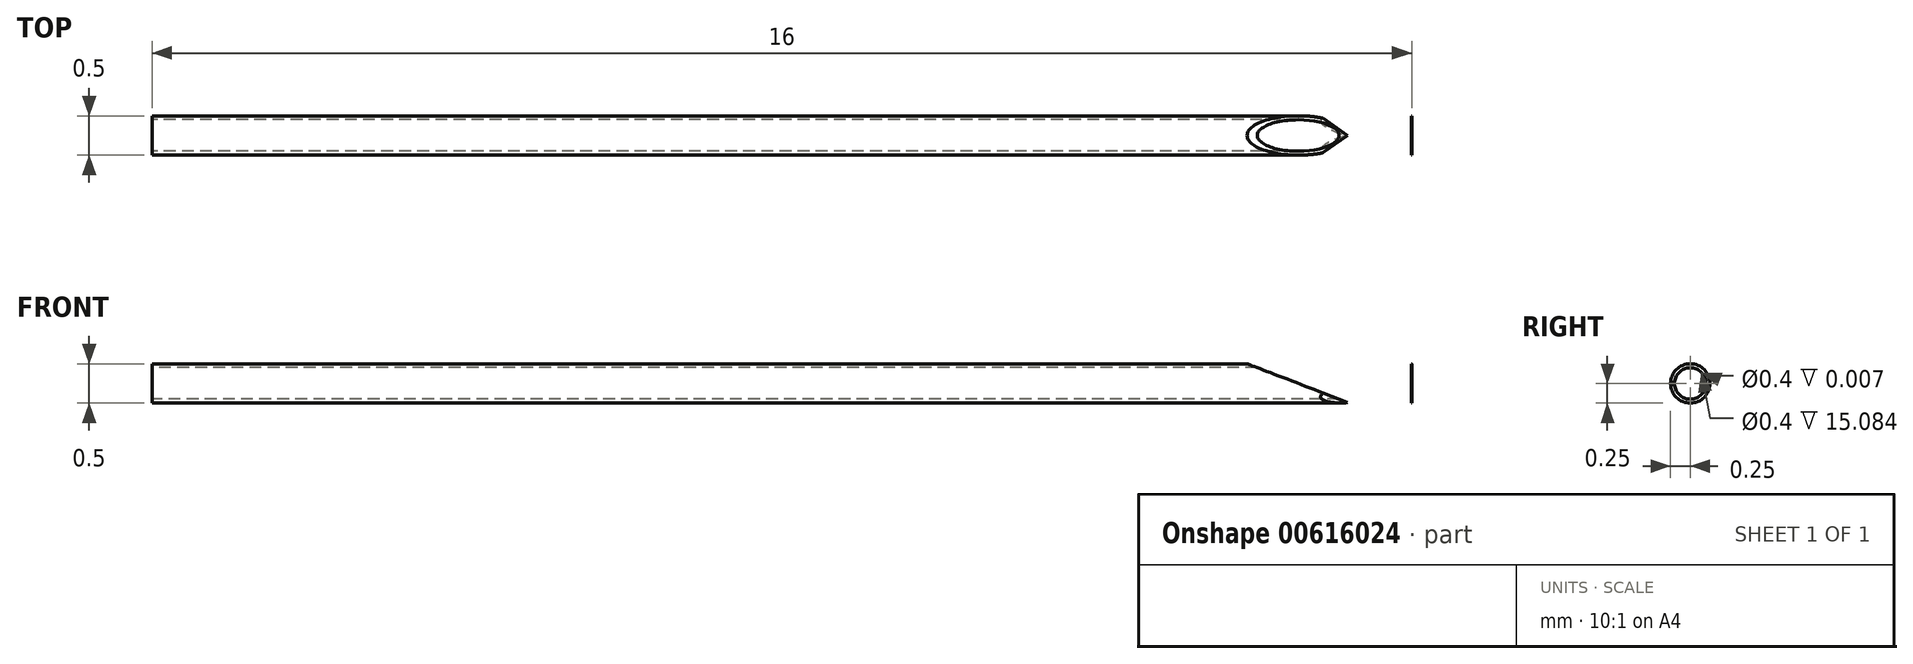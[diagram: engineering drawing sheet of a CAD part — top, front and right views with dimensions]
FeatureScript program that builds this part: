
annotation { "Feature Type Name" : "Feature", "Feature Type Description" : "" }
export const myFeature = defineFeature(function(context is Context, id is Id, definition is map)
    precondition{}
    {
        {
            var Q0;
            Q0=qCreatedBy(makeId("Front.planeOp"),FACE);
            var sketch = newSketch(context, id + "F0", { "sketchPlane" : qUnion([Q0])});
            skLineSegment(sketch, "E0", {"start": v(-2, 0) * mm, "end": v(2.09, 0) * mm, "construction": true});
            skLineSegment(sketch, "E1", {"start": v(-1.43, 0.25) * mm, "end": v(14.57, 0.25) * mm});
            skLineSegment(sketch, "E2", {"start": v(14.57, 0.25) * mm, "end": v(14.57, 0.2) * mm});
            skLineSegment(sketch, "E3", {"start": v(-1.43, 0.2) * mm, "end": v(-1.43, 0.25) * mm});
            skLineSegment(sketch, "E4", {"start": v(14.57, 0.2) * mm, "end": v(-1.43, 0.2) * mm});
            skPoint(sketch, "E5.orphan", {"position": v(-1.43, 0) * mm});
            skPoint(sketch, "E6.orphan", {"position": v(14.57, 0) * mm});
            skSolve(sketch);
        }
        {
            var Q0;
            Q0=qSketchRegion(id+"F0",true);
            var Q1;
            Q1=sQuery(id+"F0.wireOp",EDGE,"E0");
            revolve(context, id + "F1", {"entities" : qUnion([Q0]), "axis" : qUnion([Q1]), "revolveType" : RevolveType.FULL});
        }
        {
            var Q0;
            Q0=qCreatedBy(makeId("Front.planeOp"),FACE);
            var sketch = newSketch(context, id + "F2", { "sketchPlane" : qUnion([Q0])});
            skLineSegment(sketch, "E7", {"start": v(10.2, 1.12) * mm, "end": v(14.57, -0.55) * mm});
            skLineSegment(sketch, "E8", {"start": v(14.57, -0.55) * mm, "end": v(14.57, 1.12) * mm});
            skLineSegment(sketch, "E9", {"start": v(14.57, 1.12) * mm, "end": v(10.2, 1.12) * mm});
            skSolve(sketch);
        }
        {
            var Q0;
            Q0=qSketchRegion(id+"F2",true);
            extrude(context, id + "F3", {"entities" : qUnion([Q0]), "operationType" : NewBodyOperationType.REMOVE, "oppositeDirection" : true, "depth" : 25 * mm, "offsetDistance" : 25 * mm, "symmetric" : true});
        }
        {
            var Q0;
            Q0=qCreatedBy(makeId("Front.planeOp"),FACE);
            var sketch = newSketch(context, id + "F4", { "sketchPlane" : qUnion([Q0])});
            skLineSegment(sketch, "E10", {"start": v(13.68, -0.27) * mm, "end": v(14.22, -0.27) * mm});
            skLineSegment(sketch, "E11", {"start": v(14.22, -0.27) * mm, "end": v(14.22, -0.07) * mm});
            skLineSegment(sketch, "E12", {"start": v(14.22, -0.07) * mm, "end": v(13.68, -0.27) * mm});
            skSolve(sketch);
        }
        {
            var Q0;
            Q0 = qSketchRegion(id + "F4", true);
            extrude(context, id + "F5", {"entities" : qUnion([Q0]), "operationType" : NewBodyOperationType.REMOVE, "flatOperationType" : FlatOperationType.REMOVE, "depth" : 25 * mm, "offsetDistance" : 25 * mm, "hasDraft" : true, "draftAngle" : 45 * degree, "domain" : OperationDomain.MODEL, "symmetric" : true});
        }
    });
